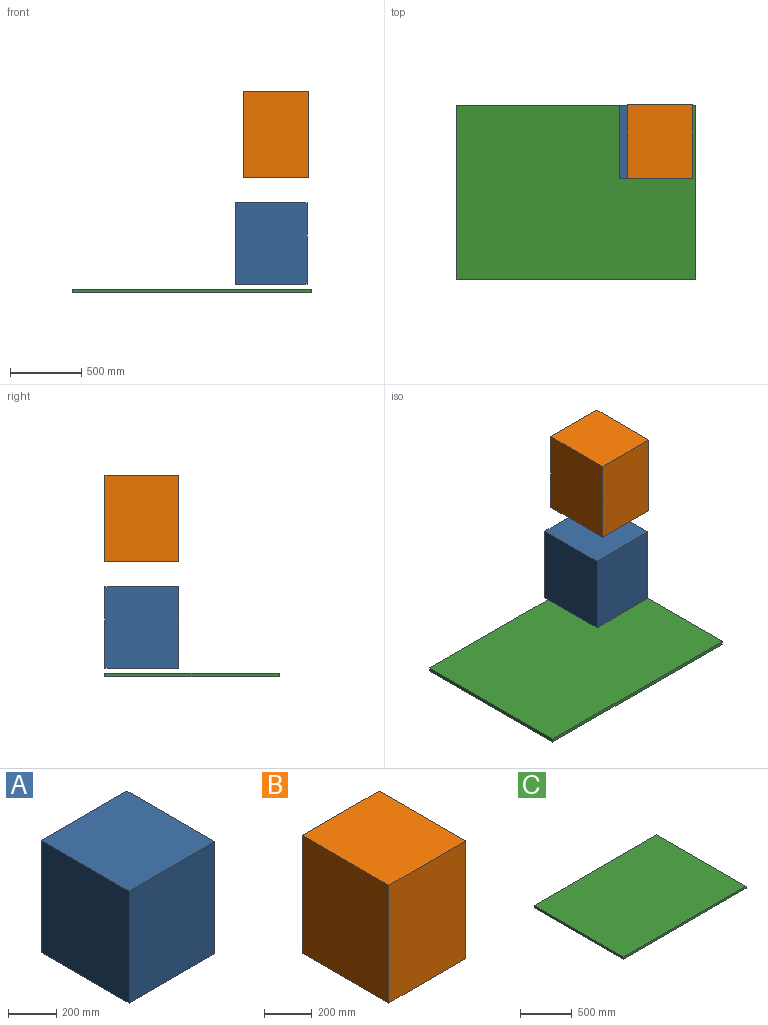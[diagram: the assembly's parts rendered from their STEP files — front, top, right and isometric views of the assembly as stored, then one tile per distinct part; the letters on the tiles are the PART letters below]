
ASSEMBLY  parts=3 mates=2
PART A: 6 faces, bbox 504x516x570 mm
  f0: plane 516x504mm, normal (0,0,1), area 260064mm2, adj f1,f3,f4,f5
  f1: plane 570x516mm, normal (-1,0,0), area 294120mm2, adj f0,f2,f4,f5
  f2: plane 516x504mm, normal (0,0,-1), area 260064mm2, adj f1,f3,f4,f5
  f3: plane 570x516mm, normal (1,0,0), area 294120mm2, adj f0,f2,f4,f5
  f4: plane 570x504mm, normal (0,-1,0), area 287280mm2, adj f0,f1,f2,f3
  f5: plane 570x504mm, normal (0,1,0), area 287280mm2, adj f0,f1,f2,f3
PART B: 6 faces, bbox 457.2x515.1x606.6 mm
  f0: plane 606.55x515.11mm, normal (1,0,0), area 312442.2mm2, adj f1,f3,f4,f5
  f1: plane 606.55x457.2mm, normal (0,1,0), area 277315.6mm2, adj f0,f2,f4,f5
  f2: plane 606.55x515.11mm, normal (-1,0,0), area 312442.2mm2, adj f1,f3,f4,f5
  f3: plane 606.55x457.2mm, normal (0,-1,0), area 277315.6mm2, adj f0,f2,f4,f5
  f4: plane 515.11x457.2mm, normal (0,0,1), area 235509.2mm2, adj f0,f1,f2,f3
  f5: plane 515.11x457.2mm, normal (0,0,-1), area 235509.2mm2, adj f0,f1,f2,f3
PART C: 6 faces, bbox 1676.4x1219.2x25.4 mm
  f0: plane 1219.2x25.4mm, normal (1,0,0), area 30967.7mm2, adj f1,f3,f4,f5
  f1: plane 1676.4x25.4mm, normal (0,1,0), area 42580.6mm2, adj f0,f2,f4,f5
  f2: plane 1219.2x25.4mm, normal (-1,0,0), area 30967.7mm2, adj f1,f3,f4,f5
  f3: plane 1676.4x25.4mm, normal (0,-1,0), area 42580.6mm2, adj f0,f2,f4,f5
  f4: plane 1676.4x1219.2mm, normal (0,0,1), area 2043866.9mm2, adj f0,f1,f2,f3
  f5: plane 1676.4x1219.2mm, normal (0,0,-1), area 2043866.9mm2, adj f0,f1,f2,f3
PLACE A t=(1152.52,1216.34,152.66)mm
PLACE B t=(1187.25,1216.78,916.18)mm
PLACE C t=(598.8,864.74,-192.03)mm fixed
MATE planar A.f5 <-> C.f1  axis (0,1,0) through (1152.52,1474.34,152.66)mm
MATE planar B.f1 <-> C.f1  axis (0,1,0) through (958.65,1474.34,916.18)mm
